# Revit family: P200921MX-030c_MFI2269FR_BWZ
name_source: partatom
category: Specialty Equipment
units: mm (PartAtom-declared; Revit-internal decimal feet)

## family parameters
Always vertical = No
Cut with Voids When Loaded = No
Enable Cutting in Views = No
Maintain Annotation Orientation = No
Part Type = Normal
Room Calculation Point = No
Round Connector Dimension = Use Diameter
Shared = No
Work Plane-Based = No

## types (3) — shared parameters
Amps = 0 A
Clearance Material = ARCAT - Clearance
Default Elevation = 0"
Depth = 34 1/4"
Description = 33- Inch Wide French Door Refrigerator with Beverage Chiller™ Compartment - 22 Cu. Ft.
Réfrigérateur à portes françaises, 33 po,  22 pi3
Dimension Guide = http://access.whirlpool.com Guide&sku=MFI2269FRW&language=EN
http://access.whirlpool.com Guide&sku=MFI2269FRW&language=EN
Energy Guide = http://access.whirlpool.com Guide&sku=MFI2269FRW&language=EN
http://access.whirlpool.com Guide&sku=MFI2269FRW&language=EN
Family Name = Refrigeration
Feature 1 = Fingerprint Resistant Stainless Steel
Acier inoxydable résistant aux traces de doigts
Feature 2 = PowerCold® Feature
Fonction PowerCold™
Feature 3 = Beverage Chiller™ Compartment
Compartiment pour boissons Beverage Chiller™
Glass Material = ARCAT - Glass - Tempered - Black
Height = 70"
Manufacturer = Maytag
Voltage = 0 V
Width = 32 5/8"

## per-type parameters (varying)
| type | Accent Material | Body Material | Display Panel Material | Door Material | Handle Material | Water Slot Material |
| MFI2269FRZ | ARCAT - Plastic - Gray | ARCAT - Metal - Steel -Gray | ARCAT - Metal - Steel -Gray Light | ARCAT - Metal - Steel - Stainless | ARCAT - Metal - Steel -Gray Light | ARCAT - Plastic Black Light |
| MFI2269FRB | ARCAT - Metal - Steel -Black - Dark | ARCAT - Metal - Steel -Black Light | ARCAT - Metal - Steel -Black - Dark | ARCAT - Metal - Steel -Black | ARCAT - Metal - Steel -Black - Dark | ARCAT - Plastic, ABS - Black |
| MFI2269FRW | ARCAT - Metal - Steel -White | ARCAT - Metal - Steel -White | ARCAT - Metal - Steel -White | ARCAT - Metal - Steel -White | ARCAT - Metal - Steel -White | ARCAT - Plastic - White |

note: column(s) folded — value = type name in every type: Model

## geometry (parser evidence)
native form markers: Sweep x5
no freeform markers — native parametric forms only
